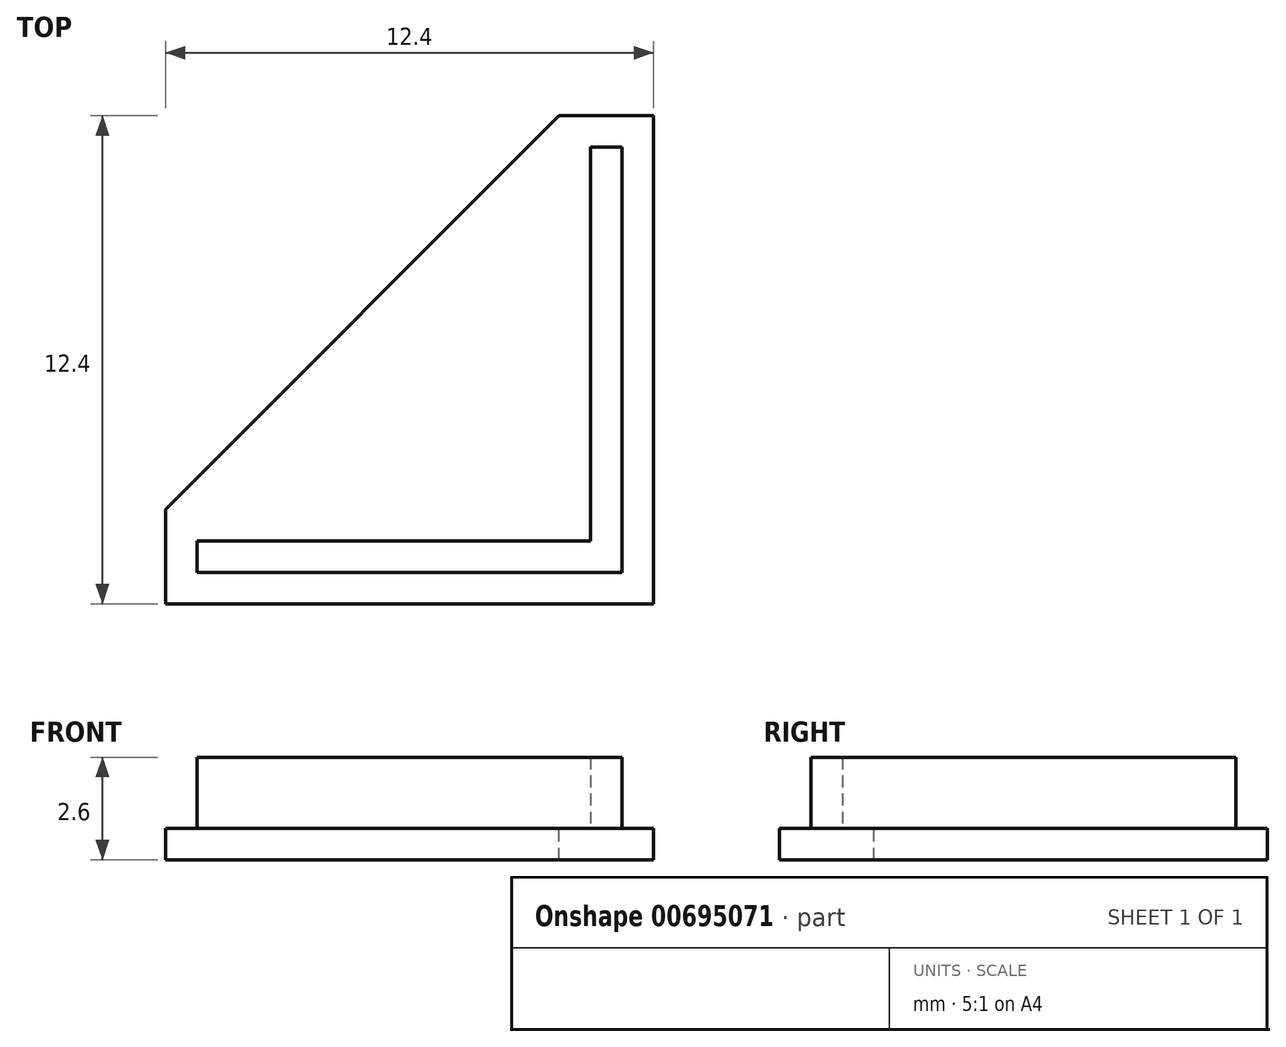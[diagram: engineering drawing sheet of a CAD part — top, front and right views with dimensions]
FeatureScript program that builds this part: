
annotation { "Feature Type Name" : "Feature", "Feature Type Description" : "" }
export const myFeature = defineFeature(function(context is Context, id is Id, definition is map)
    precondition{}
    {
        {
            var Q0;
            Q0=qCreatedBy(makeId("Top.planeOp"),FACE);
            var sketch = newSketch(context, id + "F0", { "sketchPlane" : qUnion([Q0])});
            skLineSegment(sketch, "E0", {"start": v(-0.4, 0.4) * mm, "end": v(-0.4, 10.4) * mm});
            skLineSegment(sketch, "E1", {"start": v(-0.4, 10.4) * mm, "end": v(0.4, 10.4) * mm});
            skLineSegment(sketch, "E2", {"start": v(0.4, 10.4) * mm, "end": v(0.4, 0.4) * mm});
            skLineSegment(sketch, "E3", {"start": v(0.4, 0.4) * mm, "end": v(10.4, 0.4) * mm});
            skLineSegment(sketch, "E4", {"start": v(10.4, 0.4) * mm, "end": v(10.4, -0.4) * mm});
            skLineSegment(sketch, "E5", {"start": v(10.4, -0.4) * mm, "end": v(0.4, -0.4) * mm});
            skLineSegment(sketch, "E6", {"start": v(0.4, -0.4) * mm, "end": v(0.4, -10.4) * mm});
            skLineSegment(sketch, "E7", {"start": v(0.4, -10.4) * mm, "end": v(-0.4, -10.4) * mm});
            skLineSegment(sketch, "E8", {"start": v(-0.4, -10.4) * mm, "end": v(-0.4, -0.4) * mm});
            skLineSegment(sketch, "E9", {"start": v(-0.4, -0.4) * mm, "end": v(-10.4, -0.4) * mm});
            skLineSegment(sketch, "E10", {"start": v(-10.4, -0.4) * mm, "end": v(-10.4, 0.4) * mm});
            skLineSegment(sketch, "E11", {"start": v(-10.4, 0.4) * mm, "end": v(-0.4, 0.4) * mm});
            skPoint(sketch, "E12", {"position": v(0, 10.4) * mm});
            skPoint(sketch, "E13", {"position": v(-10.4, 0) * mm});
            skLineSegment(sketch, "E14.0", {"start": v(-11.2, -1.2) * mm, "end": v(-11.2, 1.2) * mm});
            skLineSegment(sketch, "E14.1", {"start": v(1.2, 1.2) * mm, "end": v(11.2, 1.2) * mm});
            skLineSegment(sketch, "E14.2", {"start": v(1.2, 11.2) * mm, "end": v(1.2, 1.2) * mm});
            skLineSegment(sketch, "E14.3", {"start": v(-1.2, 11.2) * mm, "end": v(1.2, 11.2) * mm});
            skLineSegment(sketch, "E14.4", {"start": v(-1.2, 1.2) * mm, "end": v(-1.2, 11.2) * mm});
            skLineSegment(sketch, "E14.5", {"start": v(11.2, 1.2) * mm, "end": v(11.2, -1.2) * mm});
            skLineSegment(sketch, "E14.6", {"start": v(-11.2, 1.2) * mm, "end": v(-1.2, 1.2) * mm});
            skLineSegment(sketch, "E14.7", {"start": v(11.2, -1.2) * mm, "end": v(1.2, -1.2) * mm});
            skLineSegment(sketch, "E14.8", {"start": v(1.2, -1.2) * mm, "end": v(1.2, -11.2) * mm});
            skLineSegment(sketch, "E14.9", {"start": v(1.2, -11.2) * mm, "end": v(-1.2, -11.2) * mm});
            skLineSegment(sketch, "E14.10", {"start": v(-1.2, -11.2) * mm, "end": v(-1.2, -1.2) * mm});
            skLineSegment(sketch, "E14.11", {"start": v(-1.2, -1.2) * mm, "end": v(-11.2, -1.2) * mm});
            skLineSegment(sketch, "E15", {"start": v(-11.2, 1.2) * mm, "end": v(-1.2, 11.2) * mm});
            skLineSegment(sketch, "E16", {"start": v(1.2, 11.2) * mm, "end": v(11.2, 1.2) * mm});
            skLineSegment(sketch, "E17", {"start": v(11.2, -1.2) * mm, "end": v(1.2, -11.2) * mm});
            skLineSegment(sketch, "E18", {"start": v(-1.2, -11.2) * mm, "end": v(-11.2, -1.2) * mm});
            skLineSegment(sketch, "E19", {"start": v(-1.2, -1.2) * mm, "end": v(1.2, -1.2) * mm});
            skLineSegment(sketch, "E20", {"start": v(-0.4, -0.4) * mm, "end": v(0.4, -0.4) * mm});
            skLineSegment(sketch, "E21", {"start": v(1.2, 1.2) * mm, "end": v(1.2, -1.2) * mm});
            skLineSegment(sketch, "E22", {"start": v(0.4, 0.4) * mm, "end": v(0.4, -0.4) * mm});
            skSolve(sketch);
        }
        {
            var Q0;
            Q0=makeQuery(id+"F0.imprint","IMPRINT",FACE,{"disambiguationData":[TD([[makeQuery(id+"F0.imprint","IMPRINT",EDGE,{"derivedFrom":sQuery(id+"F0.wireOp",EDGE,"E0")}),-1.0]])]});
            extrude(context, id + "F1", {"entities" : qUnion([Q0]), "depth" : 1.8 * mm, "offsetDistance" : 25 * mm});
        }
        {
            var Q0;
            Q0=makeQuery(id+"F0.imprint","IMPRINT",FACE,{"disambiguationData":[TD([[makeQuery(id+"F0.imprint","IMPRINT",EDGE,{"derivedFrom":sQuery(id+"F0.wireOp",EDGE,"E14.4")}),1.0]])]});
            var Q1;
            Q1=makeQuery(id+"F0.imprint","IMPRINT",FACE,{"disambiguationData":[TD([[makeQuery(id+"F0.imprint","IMPRINT",EDGE,{"derivedFrom":sQuery(id+"F0.wireOp",EDGE,"E0")}),1.0]])]});
            var Q2;
            Q2=makeQuery(id+"F1.opExtrude","CAP_FACE",FACE,{"disambiguationData":[OSD([sQuery(id+"F0.wireOp",EDGE,"E0"),sQuery(id+"F0.wireOp",EDGE,"E1"),sQuery(id+"F0.wireOp",EDGE,"E2"),sQuery(id+"F0.wireOp",EDGE,"E3"),sQuery(id+"F0.wireOp",EDGE,"E4"),sQuery(id+"F0.wireOp",EDGE,"E5"),sQuery(id+"F0.wireOp",EDGE,"E6"),sQuery(id+"F0.wireOp",EDGE,"E7"),sQuery(id+"F0.wireOp",EDGE,"E8"),sQuery(id+"F0.wireOp",EDGE,"E9"),sQuery(id+"F0.wireOp",EDGE,"E10"),sQuery(id+"F0.wireOp",EDGE,"E11")])],"isStart":false});
            var Q3;
            Q3=makeQuery(id+"F0.imprint","IMPRINT",FACE,{"disambiguationData":[TD([[makeQuery(id+"F0.imprint","IMPRINT",EDGE,{"derivedFrom":sQuery(id+"F0.wireOp",EDGE,"E0")}),-1.0]])]});
            var Q4;
            {var subQ0=sQuery(id+"F0.wireOp",EDGE,"E20");Q4=makeQuery(id+"F0.imprint","IMPRINT",FACE,{"disambiguationData":[TD([[makeQuery(id+"F0.imprint","IMPRINT",EDGE,{"derivedFrom":subQ0}),-1.0]])]});}
            var Q5;
            {var subQ0=sQuery(id+"F0.wireOp",EDGE,"E22");Q5=makeQuery(id+"F0.imprint","IMPRINT",FACE,{"disambiguationData":[TD([[makeQuery(id+"F0.imprint","IMPRINT",EDGE,{"derivedFrom":subQ0}),1.0]])]});}
            var Q6;
            {var subQ1=sQuery(id+"F0.wireOp",EDGE,"E5");var subQ3=sQuery(id+"F0.wireOp",EDGE,"E21");var subQ4=makeQuery(id+"F0.imprint","INTERSECT",VERTEX,{"derivedFrom":[subQ1,subQ3]});Q6=makeQuery(id+"F0.imprint","IMPRINT",FACE,{"disambiguationData":[TD([[makeQuery(id+"F0.imprint","IMPRINT",EDGE,{"disambiguationData":[TD([[subQ4,-1.0]])],"derivedFrom":subQ1}),1.0]])]});}
            extrude(context, id + "F2", {"entities" : qUnion([Q0, Q1, Q2, Q3, Q4, Q5, Q6]), "operationType" : NewBodyOperationType.ADD, "oppositeDirection" : true, "depth" : 0.8 * mm, "offsetDistance" : 25 * mm});
        }
    });
